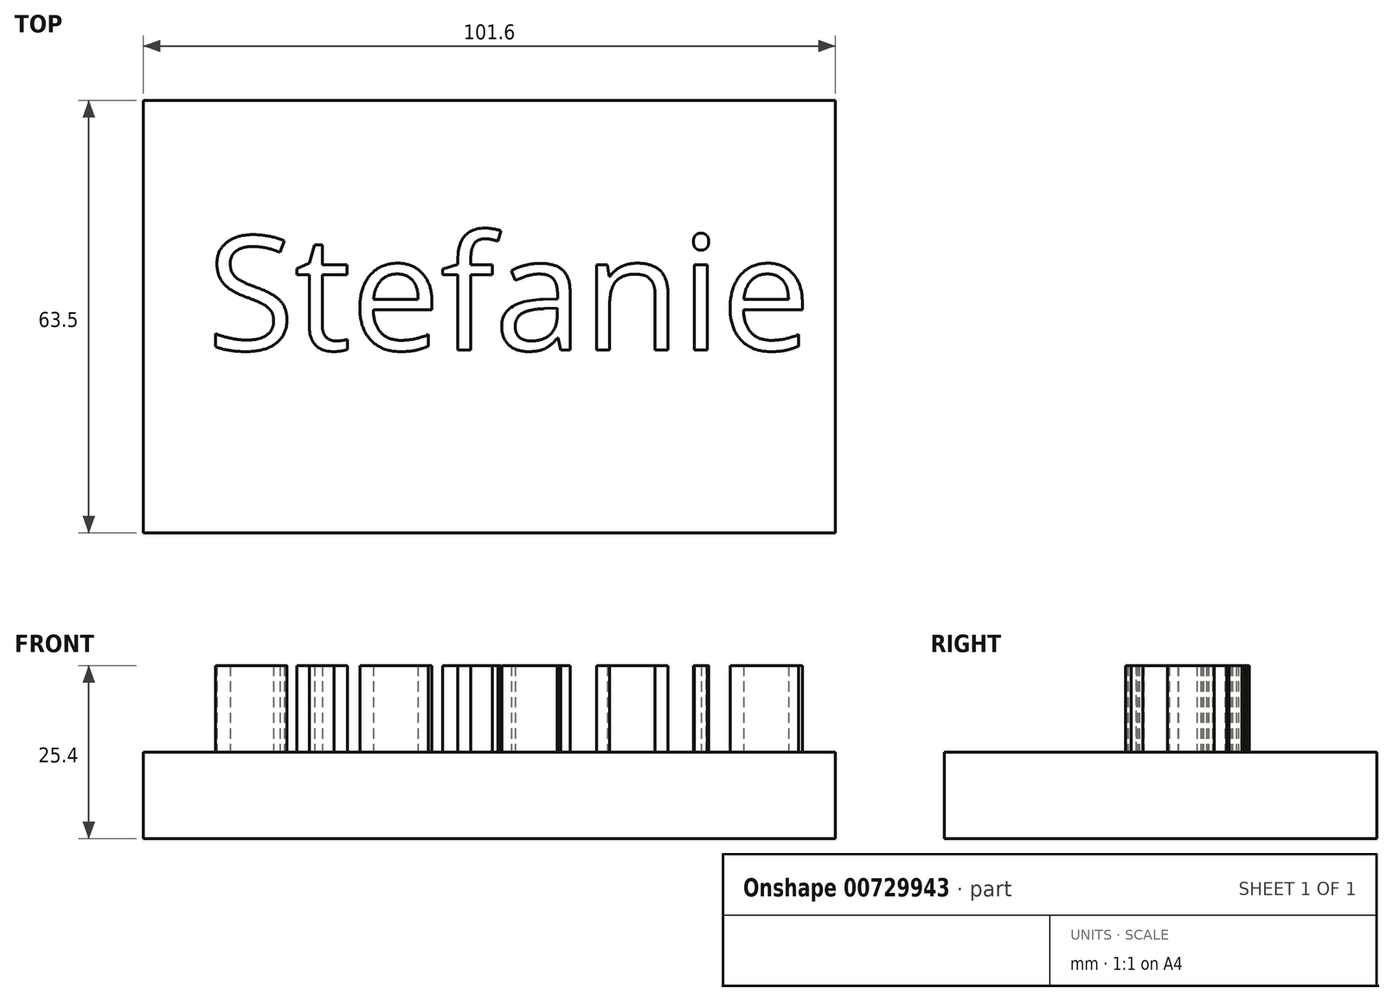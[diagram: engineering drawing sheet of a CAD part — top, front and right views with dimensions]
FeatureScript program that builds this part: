
annotation { "Feature Type Name" : "Feature", "Feature Type Description" : "" }
export const myFeature = defineFeature(function(context is Context, id is Id, definition is map)
    precondition{}
    {
        {
            var Q0;
            Q0=qCreatedBy(makeId("Top.planeOp"),FACE);
            var sketch = newSketch(context, id + "F0", { "sketchPlane" : qUnion([Q0])});
            skLineSegment(sketch, "E0.bottom", {"start": v(50.8, -31.75) * mm, "end": v(-50.8, -31.75) * mm});
            skLineSegment(sketch, "E0.top", {"start": v(50.8, 31.75) * mm, "end": v(-50.8, 31.75) * mm});
            skLineSegment(sketch, "E0.left", {"start": v(50.8, -31.75) * mm, "end": v(50.8, 31.75) * mm});
            skLineSegment(sketch, "E0.right", {"start": v(-50.8, -31.75) * mm, "end": v(-50.8, 31.75) * mm});
            skPoint(sketch, "E0.middle", {"position": v(0, 0) * mm});
            skSolve(sketch);
        }
        {
            var Q0;
            Q0=makeQuery(id+"F0.imprint","IMPRINT",FACE,{"disambiguationData":[TD([[makeQuery(id+"F0.imprint","IMPRINT",EDGE,{"derivedFrom":sQuery(id+"F0.wireOp",EDGE,"E0.bottom")}),-1.0]])]});
            extrude(context, id + "F1", {"entities" : qUnion([Q0]), "endBound" : BoundingType.SYMMETRIC, "depth" : 12.7 * mm, "offsetDistance" : 25.4 * mm});
        }
        {
            var Q0;
            Q0=makeQuery(id+"F1.opExtrude","CAP_FACE",FACE,{"disambiguationData":[OSD([sQuery(id+"F0.wireOp",EDGE,"E0.bottom"),sQuery(id+"F0.wireOp",EDGE,"E0.top"),sQuery(id+"F0.wireOp",EDGE,"E0.left"),sQuery(id+"F0.wireOp",EDGE,"E0.right")])],"isStart":false});
            var sketch = newSketch(context, id + "F2", { "sketchPlane" : qUnion([Q0])});
            skText(sketch, "E1", { "text": "Stefanie", "fontName": "OpenSans-Regular.ttf"});
            const initialGuessF2  = {"E1": [-0.04143, -0.0049, 1, 0, 0.01685]};
            skSetInitialGuess(sketch, initialGuessF2);
            skSolve(sketch);
        }
        {
            var Q0;
            Q0 = qSketchRegion(id + "F2", true);
            extrude(context, id + "F3", {"entities" : qUnion([Q0]), "operationType" : NewBodyOperationType.ADD, "depth" : 12.7 * mm, "offsetDistance" : 25.4 * mm});
        }
    });
